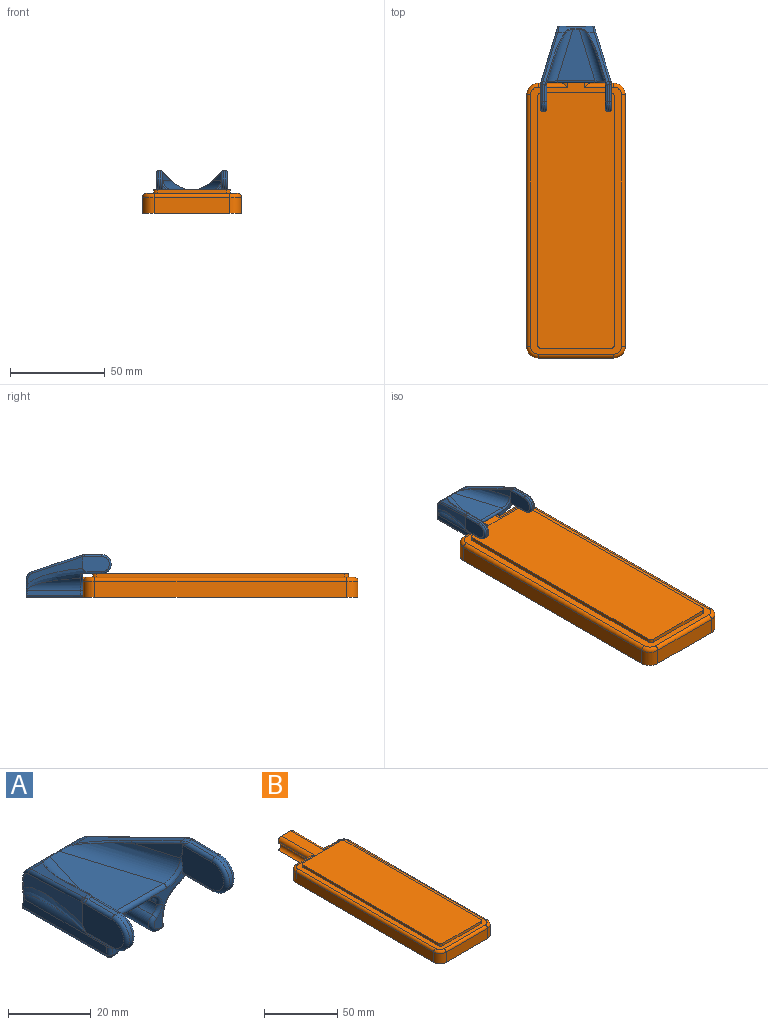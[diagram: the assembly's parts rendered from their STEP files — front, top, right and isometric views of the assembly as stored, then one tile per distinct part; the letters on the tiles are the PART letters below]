
ASSEMBLY  parts=2 mates=1
PART A: 97 faces, bbox 40.7x46.6x23.7 mm
  f0: plane 13.67x11.82mm, normal (0,-1,0), area 32.4mm2, adj f20,f66,f75,f78,f80,f81,f82,f83
  f1: plane 8.9x4.43mm, normal (0,1,0), area 23.4mm2, adj f10,f11,f12,f13,f17,f42,f43,f45
  f2: plane 27.26x19.94mm, normal (0,0,1), area 317.2mm2, adj f39,f40,f78,f92
  f3: plane 28.88x2.56mm, normal (1,0,0), area 71.1mm2, adj f16,f30,f61,f71
  f4: plane 28.88x2.56mm, normal (-1,0,0), area 71.1mm2, adj f17,f31,f43,f85
  f5: plane 29x1mm, normal (0,0,-1), area 29mm2, adj f6,f15,f16,f73
  f6: cylinder r=2.75mm len=29mm, axis (0,1,0), area 206.8mm2, adj f5,f7,f15,f74
  f7: cylinder r=3mm len=29mm, axis (0,1,0), area 86.7mm2, adj f6,f8,f15,f77
  f8: cylinder r=3mm len=29mm, axis (0,1,0), area 134mm2, adj f7,f9,f15,f42,f79
  f9: plane 28.74x9mm, normal (0,0,-1), area 258.6mm2, adj f8,f10,f42,f78
  f10: cylinder r=3mm len=29mm, axis (0,1,0), area 134mm2, adj f1,f9,f11,f42,f80
  f11: cylinder r=3mm len=29mm, axis (0,1,0), area 86.7mm2, adj f1,f10,f12,f81
  f12: cylinder r=2.75mm len=29mm, axis (0,1,0), area 206.8mm2, adj f1,f11,f13,f82
  f13: plane 29x1mm, normal (0,0,-1), area 29mm2, adj f1,f12,f17,f83
  f14: plane 13.67x11.82mm, normal (0,-1,0), area 32.4mm2, adj f26,f65,f69,f70,f71,f73,f74,f76
  f15: plane 8.9x4.43mm, normal (0,1,0), area 23.4mm2, adj f5,f6,f7,f8,f16,f42,f60,f61
  f16: cylinder r=1mm len=29mm, axis (0,1,0), area 45.5mm2, adj f3,f5,f15,f61,f72
  f17: cylinder r=1mm len=29mm, axis (0,-1,0), area 45.5mm2, adj f1,f4,f13,f43,f84
  f18: plane 29.29x14.77mm, normal (-0.96,0.29,0), area 124.4mm2, adj f22,f36,f47,f49,f50,f51,f52
  f19: plane 29.29x14.77mm, normal (0.96,0.29,0), area 124.4mm2, adj f27,f37,f56,f57,f58,f59,f60
  f20: plane 14.49x8.16mm, normal (1,0,0), area 106.1mm2, adj f0,f21,f66,f67,f68,f75
  f21: plane 13.83x4.64mm, normal (0.96,-0.29,0), area 30mm2, adj f20,f40,f68,f75,f88,f89
  f22: plane 14.5x8.5mm, normal (-1,0,0), area 104.5mm2, adj f18,f36,f44,f46,f48,f50
  f23: plane 9.19x1.14mm, normal (0,0,1), area 10.4mm2, adj f34,f41,f48,f68
  f24: plane 11.21x1.14mm, normal (0,0,-1), area 11.7mm2, adj f36,f41,f44,f66,f87
  f25: plane 13.83x4.64mm, normal (-0.96,-0.29,0), area 30mm2, adj f26,f39,f63,f76,f95,f96
  f26: plane 14.49x8.16mm, normal (-1,0,0), area 106.1mm2, adj f14,f25,f63,f64,f65,f76
  f27: plane 14.5x8.5mm, normal (1,0,0), area 104.5mm2, adj f19,f37,f53,f54,f55,f56
  f28: plane 9.19x1.14mm, normal (0,0,1), area 10.4mm2, adj f35,f38,f55,f63
  f29: plane 11.21x1.14mm, normal (0,0,-1), area 11.7mm2, adj f37,f38,f53,f65,f69
  f30: cylinder r=7mm len=28mm, axis (0,1,0), area 164.2mm2, adj f3,f37,f61,f70
  f31: cylinder r=7mm len=28mm, axis (0,-1,0), area 164.2mm2, adj f4,f36,f43,f86
  f32: plane 25.81x11.69mm, normal (0,0.32,0.95), area 53.1mm2, adj f35,f42,f58,f94,f95
  f33: plane 25.81x11.69mm, normal (0,0.32,0.95), area 53.1mm2, adj f34,f42,f51,f89,f90
  f34: cylinder r=5mm len=1.9mm, axis (1,0,0), area 2.5mm2, adj f23,f33,f50,f52,f68,f88
  f35: cylinder r=5mm len=1.9mm, axis (1,0,0), area 2.5mm2, adj f28,f32,f56,f57,f63,f96
  f36: bspline ~37.67x11.57mm, area 140.3mm2, adj f18,f22,f24,f31,f44,f45,f87
  f37: bspline ~35.97x11.62mm, area 140.3mm2, adj f19,f27,f29,f30,f53,f62,f69
  f38: cylinder r=5mm len=10mm, axis (-1,0,0), area 17.8mm2, adj f28,f29,f54,f64
  f39: cylinder r=5mm len=30.46mm, axis (-0.29,0.96,0), area 180.4mm2, adj f2,f25,f76,f93,f94
  f40: cylinder r=5mm len=30.46mm, axis (-0.29,-0.96,0), area 180.4mm2, adj f2,f21,f75,f90,f91
  f41: cylinder r=5mm len=10mm, axis (-1,0,0), area 17.8mm2, adj f23,f24,f46,f67
  f42: cylinder r=5mm len=19.18mm, axis (-1,0,0), area 77.4mm2, adj f1,f8,f9,f10,f15,f32,f33,f49
  f43: torus R=8mm, axis (0,1,0), area 4.3mm2, adj f1,f4,f17,f31,f45
  f44: cylinder r=1mm len=10.72mm, axis (0,-1,0), area 14.3mm2, adj f22,f24,f36,f46
  f45: bspline ~4.13x1.19mm, area 3.4mm2, adj f1,f36,f43,f47
  f46: torus R=4mm, axis (1,0,0), area 22.9mm2, adj f22,f41,f44,f48
  f47: cylinder r=1mm len=2.2mm, axis (0,0,-1), area 2.8mm2, adj f1,f18,f45,f49
  f48: cylinder r=1mm len=9.19mm, axis (0,1,0), area 14.4mm2, adj f22,f23,f46,f50
  f49: bspline ~5.1x3.92mm, area 7.8mm2, adj f18,f42,f47,f51
  f50: torus R=4mm, axis (1,0,0), area 1.3mm2, adj f18,f22,f34,f48,f52
  f51: cylinder r=1mm len=25.93mm, axis (-0.28,-0.91,0.3), area 41.9mm2, adj f18,f33,f49,f52
  f52: bspline ~1.89x1.37mm, area 1.2mm2, adj f18,f34,f50,f51
  f53: cylinder r=1mm len=10.72mm, axis (0,1,0), area 14.3mm2, adj f27,f29,f37,f54
  f54: torus R=4mm, axis (1,0,0), area 22.9mm2, adj f27,f38,f53,f55
  f55: cylinder r=1mm len=9.19mm, axis (0,-1,0), area 14.4mm2, adj f27,f28,f54,f56
  f56: torus R=4mm, axis (1,0,0), area 1.3mm2, adj f19,f27,f35,f55,f57
  f57: bspline ~1.89x1.37mm, area 1.2mm2, adj f19,f35,f56,f58
  f58: cylinder r=1mm len=25.93mm, axis (0.28,-0.91,0.3), area 41.9mm2, adj f19,f32,f57,f59
  f59: bspline ~4.89x3.92mm, area 7.8mm2, adj f19,f42,f58,f60
  f60: cylinder r=1mm len=2.2mm, axis (0,0,1), area 2.8mm2, adj f15,f19,f59,f62
  f61: torus R=8mm, axis (0,1,0), area 4.3mm2, adj f3,f15,f16,f30,f62
  f62: bspline ~2.66x1.2mm, area 3.4mm2, adj f15,f37,f60,f61
  f63: cylinder r=1mm len=10mm, axis (0,1,0), area 14.6mm2, adj f25,f26,f28,f35,f64,f96
  f64: torus R=4mm, axis (1,0,0), area 22.9mm2, adj f26,f38,f63,f65
  f65: cylinder r=1mm len=10.01mm, axis (0,-1,0), area 15.7mm2, adj f14,f26,f29,f64,f69
  f66: cylinder r=1mm len=10.01mm, axis (0,1,0), area 15.7mm2, adj f0,f20,f24,f67,f87
  f67: torus R=4mm, axis (1,0,0), area 22.9mm2, adj f20,f41,f66,f68
  f68: cylinder r=1mm len=10mm, axis (0,-1,0), area 14.6mm2, adj f20,f21,f23,f34,f67,f88
  f69: bspline ~4.58x3.65mm, area 5.7mm2, adj f14,f29,f37,f65,f70
  f70: torus R=8mm, axis (0,1,0), area 14.9mm2, adj f14,f30,f69,f71
  f71: cylinder r=1mm len=2.5mm, axis (0,0,1), area 3.9mm2, adj f3,f14,f70,f72
  f72: sphere r=1mm, area 1.6mm2, adj f16,f71,f73
  f73: cylinder r=1mm len=1mm, axis (1,0,0), area 1.6mm2, adj f5,f14,f72,f74
  f74: torus R=1.75mm, axis (0,1,0), area 9.7mm2, adj f6,f14,f73,f77
  f75: bspline ~8.83x6.27mm, area 10.8mm2, adj f0,f20,f21,f40,f78
  f76: bspline ~9.23x7.36mm, area 10.8mm2, adj f14,f25,f26,f39,f78
  f77: torus R=4mm, axis (0,1,0), area 5.3mm2, adj f7,f14,f74,f79
  f78: cylinder r=1mm len=19.94mm, axis (-1,0,0), area 45.5mm2, adj f0,f2,f9,f14,f75,f76,f79,f80
  f79: torus R=4mm, axis (0,1,0), area 8.2mm2, adj f8,f14,f77,f78
  f80: torus R=4mm, axis (0,1,0), area 8.2mm2, adj f0,f10,f78,f81
  f81: torus R=4mm, axis (0,1,0), area 5.3mm2, adj f0,f11,f80,f82
  f82: torus R=1.75mm, axis (0,1,0), area 9.7mm2, adj f0,f12,f81,f83
  f83: cylinder r=1mm len=1mm, axis (1,0,0), area 1.6mm2, adj f0,f13,f82,f84
  f84: sphere r=1mm, area 1.6mm2, adj f17,f83,f85
  f85: cylinder r=1mm len=2.5mm, axis (0,0,-1), area 3.9mm2, adj f0,f4,f84,f86
  f86: torus R=8mm, axis (0,1,0), area 14.9mm2, adj f0,f31,f85,f87
  f87: bspline ~4.58x3.65mm, area 5.7mm2, adj f0,f24,f36,f66,f86
  f88: bspline ~3.12x1.36mm, area 1.3mm2, adj f21,f34,f68,f89
  f89: cylinder r=0.5mm len=13.11mm, axis (0.28,0.91,-0.3), area 11.7mm2, adj f21,f33,f88,f90
  f90: bspline ~13.31x6.47mm, area 9.4mm2, adj f33,f40,f89,f91
  f91: bspline ~4.95x2.44mm, area 2mm2, adj f40,f42,f90,f92
  f92: cylinder r=0.5mm len=3.33mm, axis (-1,0,0), area 1.3mm2, adj f2,f42,f91,f93
  f93: bspline ~5.25x2.94mm, area 2mm2, adj f39,f42,f92,f94
  f94: bspline ~13.31x6.47mm, area 9.4mm2, adj f32,f39,f93,f95
  f95: cylinder r=0.5mm len=13.11mm, axis (-0.28,0.91,-0.3), area 11.7mm2, adj f25,f32,f94,f96
  f96: bspline ~3.12x1.36mm, area 1.3mm2, adj f25,f35,f63,f95
PART B: 36 faces, bbox 53x175.5x12.5 mm
  f0: plane 173x48mm, normal (0,0,1), area 1578.2mm2, adj f1,f8,f9,f10,f11,f15,f16,f17
  f1: plane 15x10.5mm, normal (0,1,0), area 128.5mm2, adj f0,f7,f13,f14,f32,f33,f34,f35
  f2: plane 15.25x8.5mm, normal (0,1,0), area 118.9mm2, adj f7,f14,f16,f26,f34,f35
  f3: plane 133x8.5mm, normal (-1,0,0), area 1130.5mm2, adj f7,f18,f24,f26
  f4: plane 40x8.5mm, normal (0,-1,0), area 340mm2, adj f7,f19,f22,f24
  f5: plane 133x8.5mm, normal (1,0,0), area 1130.5mm2, adj f7,f17,f20,f22
  f6: plane 15.25x8.5mm, normal (0,1,0), area 118.9mm2, adj f7,f13,f15,f20,f32,f33
  f7: plane 175x52mm, normal (0,0,-1), area 7959.1mm2, adj f1,f2,f3,f4,f5,f6,f13,f14
  f8: plane 36.5x2mm, normal (0,-1,0), area 73mm2, adj f0,f12,f28,f31
  f9: plane 131x2mm, normal (1,0,0), area 262mm2, adj f0,f12,f28,f29
  f10: plane 36.5x2mm, normal (0,1,0), area 73mm2, adj f0,f12,f29,f30
  f11: plane 131x2mm, normal (-1,0,0), area 262mm2, adj f0,f12,f30,f31
  f12: plane 135x40.5mm, normal (0,0,1), area 5464.1mm2, adj f8,f9,f10,f11,f28,f29,f30,f31
  f13: cylinder r=2.75mm len=30mm, axis (0,1,0), area 213.9mm2, adj f1,f6,f7,f33
  f14: cylinder r=2.75mm len=30mm, axis (0,1,0), area 213.9mm2, adj f1,f2,f7,f35
  f15: cylinder r=2mm len=15.5mm, axis (-1,0,0), area 43.5mm2, adj f0,f6,f21,f32
  f16: cylinder r=2mm len=15.5mm, axis (-1,0,0), area 43.5mm2, adj f0,f2,f27,f34
  f17: cylinder r=2mm len=133mm, axis (0,1,0), area 417.8mm2, adj f0,f5,f21,f23
  f18: cylinder r=2mm len=133mm, axis (0,-1,0), area 417.8mm2, adj f0,f3,f25,f27
  f19: cylinder r=2mm len=40mm, axis (1,0,0), area 125.7mm2, adj f0,f4,f23,f25
  f20: cylinder r=6mm len=8.5mm, axis (0,0,1), area 80.1mm2, adj f5,f6,f7,f21
  f21: torus R=4mm, axis (0,0,1), area 26mm2, adj f0,f15,f17,f20
  f22: cylinder r=6mm len=8.5mm, axis (0,0,-1), area 80.1mm2, adj f4,f5,f7,f23
  f23: torus R=4mm, axis (0,0,1), area 26mm2, adj f0,f17,f19,f22
  f24: cylinder r=6mm len=8.5mm, axis (0,0,1), area 80.1mm2, adj f3,f4,f7,f25
  f25: torus R=4mm, axis (0,0,1), area 26mm2, adj f0,f18,f19,f24
  f26: cylinder r=6mm len=8.5mm, axis (0,0,-1), area 80.1mm2, adj f2,f3,f7,f27
  f27: torus R=4mm, axis (0,0,1), area 26mm2, adj f0,f16,f18,f26
  f28: cylinder r=2mm len=2mm, axis (0,0,1), area 6.3mm2, adj f0,f8,f9,f12
  f29: cylinder r=2mm len=2mm, axis (0,0,-1), area 6.3mm2, adj f0,f9,f10,f12
  f30: cylinder r=2mm len=2mm, axis (0,0,1), area 6.3mm2, adj f0,f10,f11,f12
  f31: cylinder r=2mm len=2mm, axis (0,0,-1), area 6.3mm2, adj f0,f8,f11,f12
  f32: cylinder r=3mm len=32mm, axis (0,1,0), area 141.8mm2, adj f0,f1,f6,f15,f33
  f33: cylinder r=3mm len=30mm, axis (0,1,0), area 89.6mm2, adj f1,f6,f13,f32
  f34: cylinder r=3mm len=32mm, axis (0,-1,0), area 141.8mm2, adj f0,f1,f2,f16,f35
  f35: cylinder r=3mm len=30mm, axis (0,1,0), area 89.6mm2, adj f1,f2,f14,f34
PLACE A t=(0,0.53,-0.1)mm
PLACE B at identity fixed
MATE fastened B.f0 <-> A.f9  axis (0,0,1) through (0,15,0)mm
